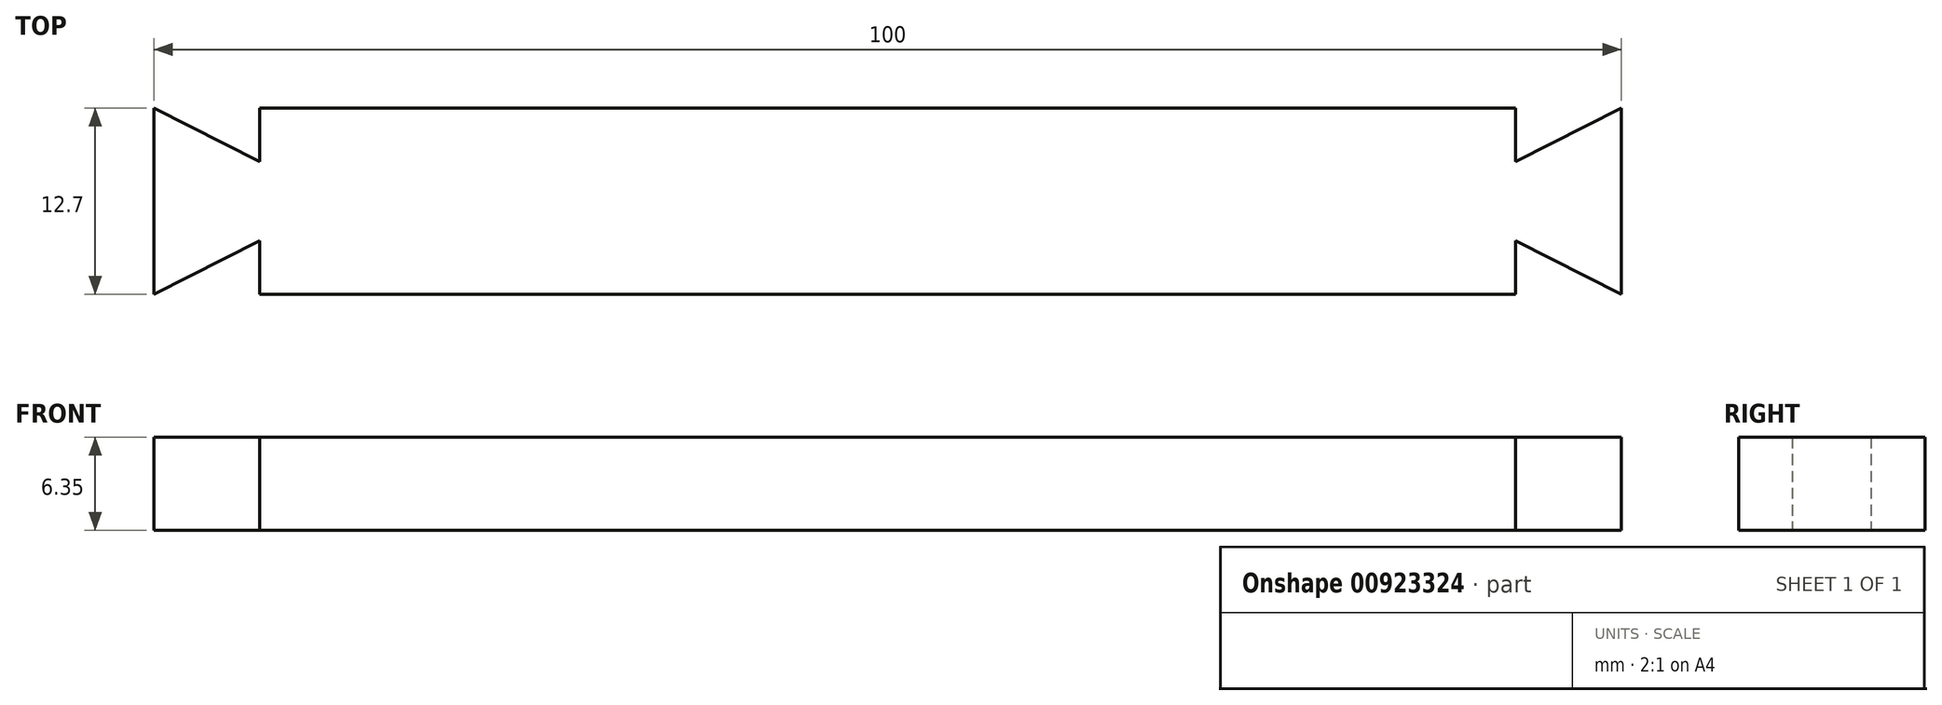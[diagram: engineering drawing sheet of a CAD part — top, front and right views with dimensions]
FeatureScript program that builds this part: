
annotation { "Feature Type Name" : "Feature", "Feature Type Description" : "" }
export const myFeature = defineFeature(function(context is Context, id is Id, definition is map)
    precondition{}
    {
        {
            var Q0;
            Q0=qCreatedBy(makeId("Top.planeOp"),FACE);
            var sketch = newSketch(context, id + "F0", { "sketchPlane" : qUnion([Q0])});
            skLineSegment(sketch, "E0.top", {"start": v(-38.2, -3.48) * mm, "end": v(-30.98, -3.48) * mm, "construction": true});
            skLineSegment(sketch, "E0.left", {"start": v(-38.2, 9.22) * mm, "end": v(-38.2, -3.48) * mm});
            skLineSegment(sketch, "E0.right", {"start": v(11.8, 9.22) * mm, "end": v(11.8, -3.48) * mm, "construction": true});
            skLineSegment(sketch, "E1.MirrorCS", {"start": v(61.8, 9.22) * mm, "end": v(54.6, 9.22) * mm, "construction": true});
            skLineSegment(sketch, "E2.MirrorCS", {"start": v(61.8, 9.22) * mm, "end": v(61.8, -3.48) * mm});
            skLineSegment(sketch, "E3.MirrorCS", {"start": v(61.8, -3.48) * mm, "end": v(54.6, -3.48) * mm, "construction": true});
            skLineSegment(sketch, "E4", {"start": v(-30.98, 9.22) * mm, "end": v(-30.98, 5.56) * mm});
            skPoint(sketch, "E5", {"position": v(-30.98, 2.87) * mm});
            skLineSegment(sketch, "E6", {"start": v(-38.2, 9.22) * mm, "end": v(-30.98, 5.56) * mm});
            skLineSegment(sketch, "E7", {"start": v(-30.98, 2.87) * mm, "end": v(-38.2, 2.87) * mm, "construction": true});
            skLineSegment(sketch, "E8", {"start": v(-30.98, 9.22) * mm, "end": v(11.8, 9.22) * mm});
            skLineSegment(sketch, "E9.MirrorCS", {"start": v(-38.2, -3.48) * mm, "end": v(-30.98, 0.18) * mm});
            skLineSegment(sketch, "E10.MirrorCS", {"start": v(-38.2, -3.48) * mm, "end": v(-38.2, 9.22) * mm});
            skLineSegment(sketch, "E11", {"start": v(-30.98, -3.48) * mm, "end": v(-30.98, -3.48) * mm});
            skLineSegment(sketch, "E12", {"start": v(-30.98, -3.48) * mm, "end": v(11.8, -3.48) * mm});
            skLineSegment(sketch, "E13.MirrorCS", {"start": v(61.8, 9.22) * mm, "end": v(54.6, 5.56) * mm});
            skLineSegment(sketch, "E14.MirrorCS", {"start": v(61.8, -3.48) * mm, "end": v(61.8, 9.22) * mm});
            skLineSegment(sketch, "E15.MirrorCS", {"start": v(61.8, -3.48) * mm, "end": v(54.6, 0.18) * mm});
            skLineSegment(sketch, "E16.MirrorCS", {"start": v(54.6, 9.22) * mm, "end": v(54.6, 5.56) * mm});
            skLineSegment(sketch, "E17", {"start": v(-30.98, 5.56) * mm, "end": v(-30.98, 0.18) * mm, "construction": true});
            skLineSegment(sketch, "E18", {"start": v(-30.98, 0.18) * mm, "end": v(-30.98, -3.48) * mm});
            skLineSegment(sketch, "E19", {"start": v(54.6, 9.22) * mm, "end": v(11.8, 9.22) * mm});
            skLineSegment(sketch, "E20", {"start": v(54.6, 5.56) * mm, "end": v(54.6, 5.56) * mm});
            skLineSegment(sketch, "E21", {"start": v(54.6, 0.18) * mm, "end": v(54.6, -3.48) * mm});
            skLineSegment(sketch, "E22", {"start": v(54.6, -3.48) * mm, "end": v(54.6, -3.48) * mm});
            skLineSegment(sketch, "E23", {"start": v(54.6, 5.56) * mm, "end": v(54.6, 0.18) * mm, "construction": true});
            skLineSegment(sketch, "E24", {"start": v(54.6, -3.48) * mm, "end": v(11.8, -3.48) * mm});
            skSolve(sketch);
        }
        {
            var Q0;
            Q0 = qSketchRegion(id + "F0", true);
            extrude(context, id + "F1", {"entities" : qUnion([Q0]), "depth" : 6.35 * mm, "offsetDistance" : 25.4 * mm});
        }
    });
